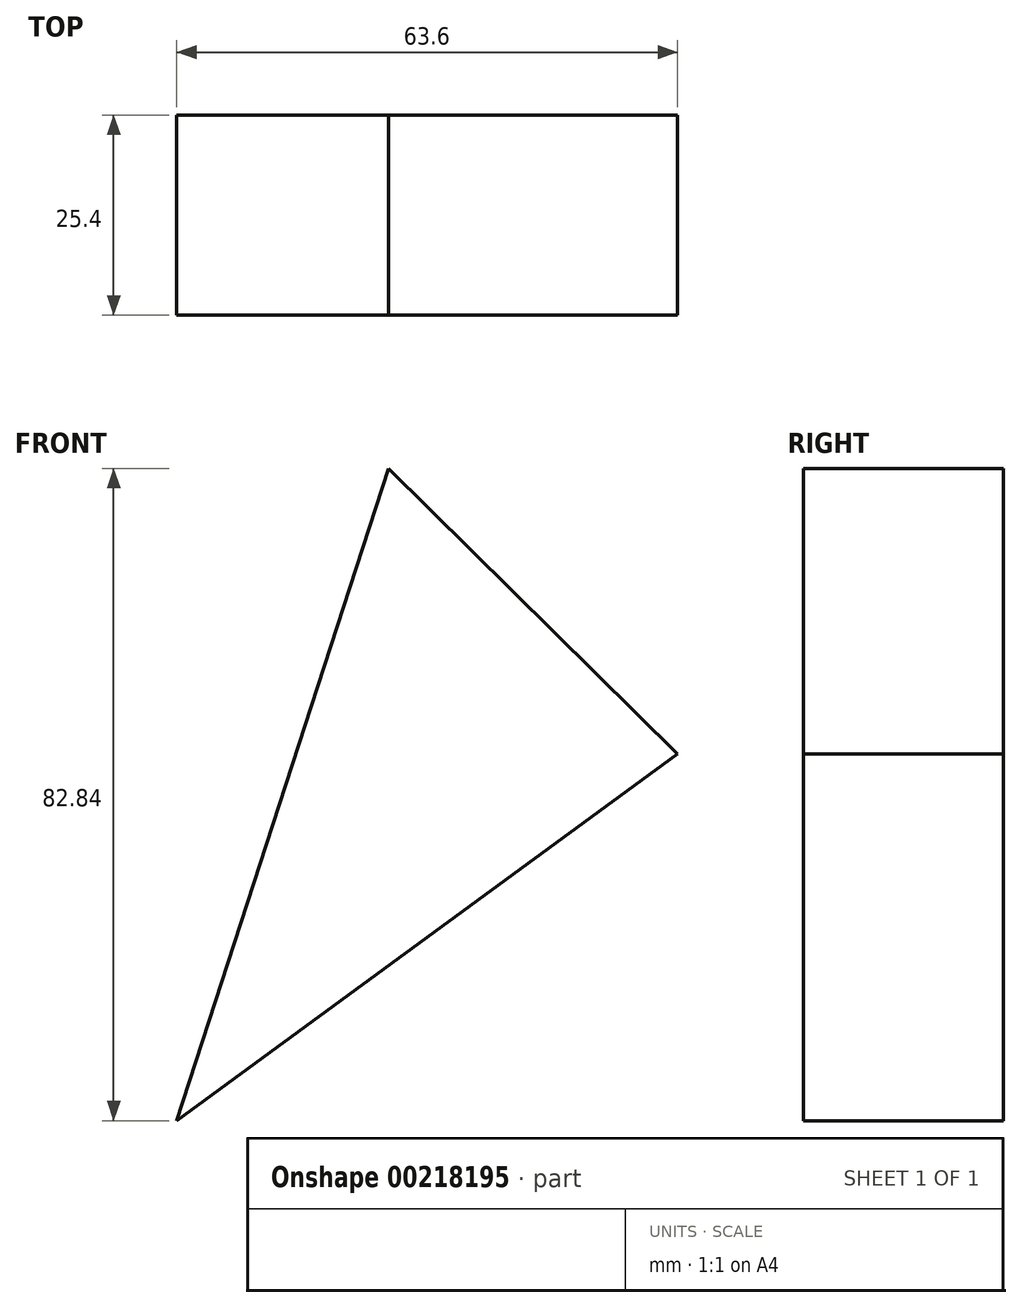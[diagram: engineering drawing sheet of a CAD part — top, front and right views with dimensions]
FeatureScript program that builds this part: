
annotation { "Feature Type Name" : "Feature", "Feature Type Description" : "" }
export const myFeature = defineFeature(function(context is Context, id is Id, definition is map)
    precondition{}
    {
        {
            var Q0;
            Q0=qCreatedBy(makeId("Front.planeOp"),FACE);
            var sketch = newSketch(context, id + "F0", { "sketchPlane" : qUnion([Q0])});
            skLineSegment(sketch, "E0", {"start": v(-46.56, 58.2) * mm, "end": v(-9.84, 21.91) * mm});
            skLineSegment(sketch, "E1", {"start": v(-9.84, 21.91) * mm, "end": v(-73.44, -24.64) * mm});
            skLineSegment(sketch, "E2", {"start": v(-73.44, -24.64) * mm, "end": v(-46.56, 58.2) * mm});
            skSolve(sketch);
        }
        {
            var Q0;
            Q0=makeQuery(id+"F0.imprint","IMPRINT",FACE,{"disambiguationData":[TD([[makeQuery(id+"F0.imprint","IMPRINT",EDGE,{"derivedFrom":sQuery(id+"F0.wireOp",EDGE,"E0")}),-1.0]])]});
            extrude(context, id + "F1", {"entities" : qUnion([Q0]), "depth" : 25.4 * mm});
        }
    });
